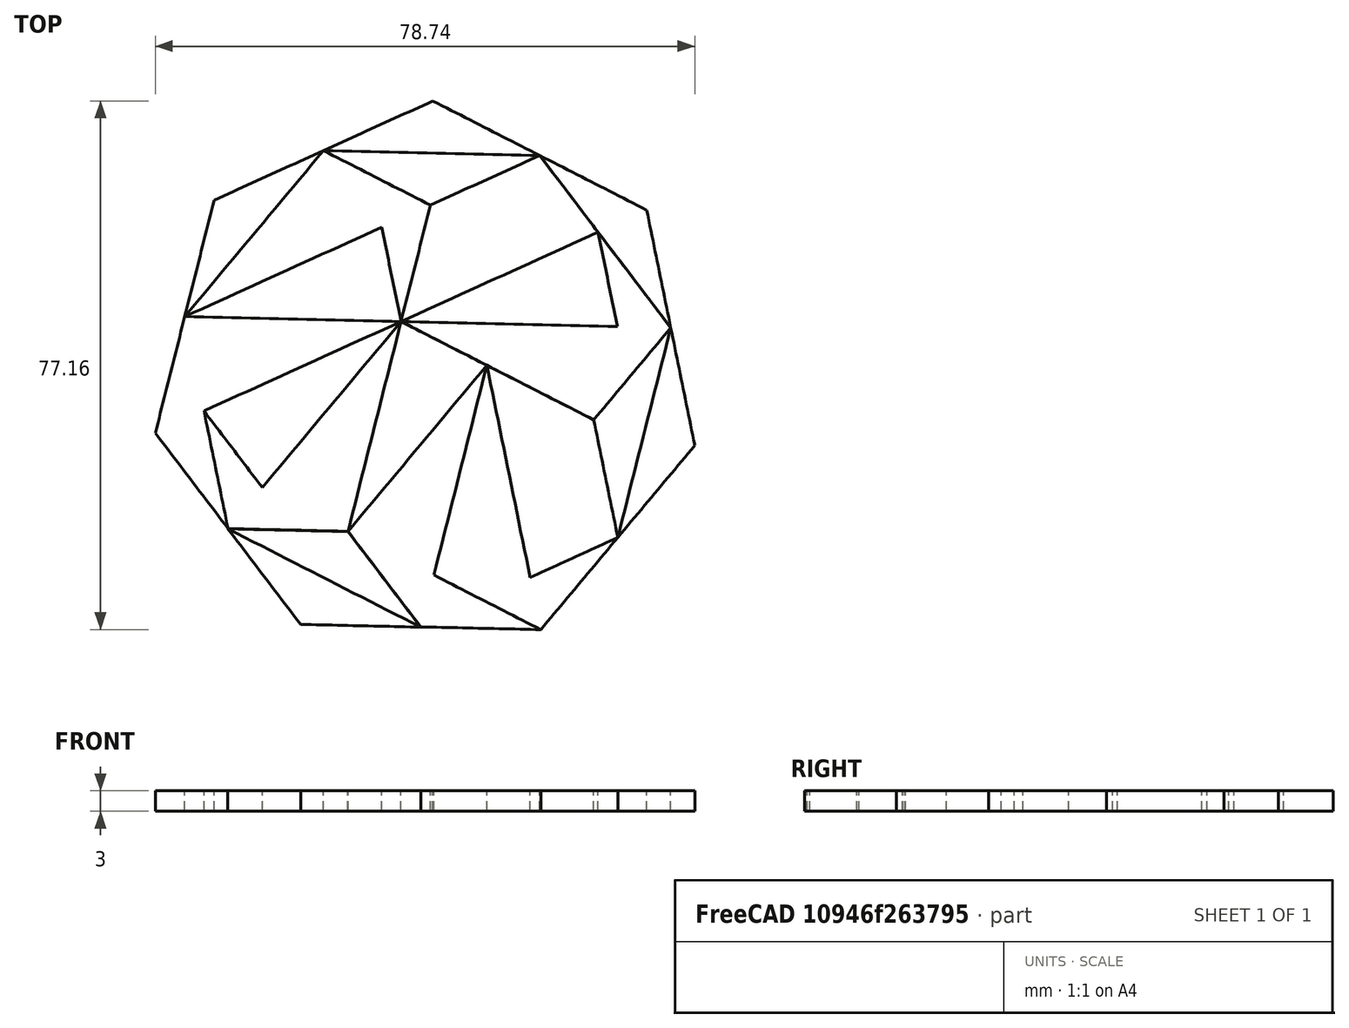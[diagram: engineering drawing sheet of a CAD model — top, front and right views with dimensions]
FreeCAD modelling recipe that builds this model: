
FCSTD DOCUMENT  (FreeCAD 0.17R13509 (Git))
Label: Puzle_Heptagono
License: CreativeCommons Attribution-ShareAlike
LicenseURL: http://creativecommons.org/licenses/by-sa/4.0/
objects: Part::Feature×20, Part::Extrusion×20
note: 40 computed .brp shape members not serialized (recipe doc carries the construction recipe); baked Part::Feature solids carry a one-line shape summary decoded from their .brp

FEATURE [Part::Feature] path28
  shape: bbox 28.13 x 38.58 x 2e-07 mm, 1 faces, 0 solids (baked)
FEATURE [Part::Feature] path34
  shape: bbox 26.85 x 38.58 x 2e-07 mm, 1 faces, 0 solids (baked)
FEATURE [Part::Feature] path40
  shape: bbox 28.76 x 30.62 x 2e-07 mm, 1 faces, 0 solids (baked)
FEATURE [Part::Feature] path46
  shape: bbox 28.76 x 24.23 x 2e-07 mm, 1 faces, 0 solids (baked)
FEATURE [Part::Feature] path52
  shape: bbox 31.57 x 13.77 x 2e-07 mm, 1 faces, 0 solids (baked)
FEATURE [Part::Feature] path58
  shape: bbox 31.57 x 13.77 x 2e-07 mm, 1 faces, 0 solids (baked)
FEATURE [Part::Feature] path64
  shape: bbox 35.86 x 30.94 x 2e-07 mm, 1 faces, 0 solids (baked)
FEATURE [Part::Feature] path70
  shape: bbox 20.25 x 30.62 x 2e-07 mm, 1 faces, 0 solids (baked)
FEATURE [Part::Feature] path76
  shape: bbox 19.12 x 30.94 x 2e-07 mm, 1 faces, 0 solids (baked)
FEATURE [Part::Feature] path82
  shape: bbox 11.24 x 30.62 x 2e-07 mm, 1 faces, 0 solids (baked)
FEATURE [Part::Feature] path88
  shape: bbox 11.24 x 30.62 x 2e-07 mm, 1 faces, 0 solids (baked)
FEATURE [Part::Feature] path94
  shape: bbox 39.37 x 27.4 x 2e-07 mm, 1 faces, 0 solids (baked)
FEATURE [Part::Feature] path100
  shape: bbox 19.12 x 25.13 x 2e-07 mm, 1 faces, 0 solids (baked)
FEATURE [Part::Feature] path106
  shape: bbox 28.76 x 24.23 x 2e-07 mm, 1 faces, 0 solids (baked)
FEATURE [Part::Feature] path112
  shape: bbox 35.86 x 24.95 x 2e-07 mm, 1 faces, 0 solids (baked)
FEATURE [Part::Feature] path124
  shape: bbox 20.25 x 24.23 x 2e-07 mm, 1 faces, 0 solids (baked)
FEATURE [Part::Feature] path118
  shape: bbox 31.9 x 20.87 x 2e-07 mm, 1 faces, 0 solids (baked)
FEATURE [Part::Feature] path130
  shape: bbox 28.13 x 14.35 x 2e-07 mm, 1 faces, 0 solids (baked)
FEATURE [Part::Feature] path5263
  shape: bbox 31.57 x 7.962 x 2e-07 mm, 1 faces, 0 solids (baked)
FEATURE [Part::Feature] path5269
  shape: bbox 31.57 x 7.962 x 2e-07 mm, 1 faces, 0 solids (baked)
FEATURE [Part::Extrusion] Extrude  label="Extrude01"
  Base = -> path28
  Dir = (0,0,1)
  DirMode = 0
  FaceMakerClass = Part::FaceMakerBullseye
  LengthFwd = 3
  LengthRev = 0
  Solid = false
  Symmetric = false
FEATURE [Part::Extrusion] Extrude001  label="Extrude02"
  Base = -> path34
  Dir = (0,0,1)
  DirMode = 0
  FaceMakerClass = Part::FaceMakerBullseye
  LengthFwd = 3
  LengthRev = 0
  Solid = false
  Symmetric = false
FEATURE [Part::Extrusion] Extrude002  label="Extrude03"
  Base = -> path40
  Dir = (0,0,1)
  DirMode = 0
  FaceMakerClass = Part::FaceMakerBullseye
  LengthFwd = 3
  LengthRev = 0
  Solid = false
  Symmetric = false
FEATURE [Part::Extrusion] Extrude003  label="Extrude04"
  Base = -> path46
  Dir = (0,0,1)
  DirMode = 0
  FaceMakerClass = Part::FaceMakerBullseye
  LengthFwd = 3
  LengthRev = 0
  Solid = false
  Symmetric = false
FEATURE [Part::Extrusion] Extrude004  label="Extrude05"
  Base = -> path52
  Dir = (0,0,1)
  DirMode = 0
  FaceMakerClass = Part::FaceMakerBullseye
  LengthFwd = 3
  LengthRev = 0
  Solid = false
  Symmetric = false
FEATURE [Part::Extrusion] Extrude005  label="Extrude06"
  Base = -> path58
  Dir = (0,0,1)
  DirMode = 0
  FaceMakerClass = Part::FaceMakerBullseye
  LengthFwd = 3
  LengthRev = 0
  Solid = false
  Symmetric = false
FEATURE [Part::Extrusion] Extrude006  label="Extrude07"
  Base = -> path64
  Dir = (0,0,1)
  DirMode = 0
  FaceMakerClass = Part::FaceMakerBullseye
  LengthFwd = 3
  LengthRev = 0
  Solid = false
  Symmetric = false
FEATURE [Part::Extrusion] Extrude007  label="Extrude08"
  Base = -> path70
  Dir = (0,0,1)
  DirMode = 0
  FaceMakerClass = Part::FaceMakerBullseye
  LengthFwd = 3
  LengthRev = 0
  Solid = false
  Symmetric = false
FEATURE [Part::Extrusion] Extrude008  label="Extrude09"
  Base = -> path76
  Dir = (0,0,1)
  DirMode = 0
  FaceMakerClass = Part::FaceMakerBullseye
  LengthFwd = 3
  LengthRev = 0
  Solid = false
  Symmetric = false
FEATURE [Part::Extrusion] Extrude009  label="Extrude10"
  Base = -> path82
  Dir = (0,0,1)
  DirMode = 0
  FaceMakerClass = Part::FaceMakerBullseye
  LengthFwd = 3
  LengthRev = 0
  Solid = false
  Symmetric = false
FEATURE [Part::Extrusion] Extrude010  label="Extrude11"
  Base = -> path88
  Dir = (0,0,1)
  DirMode = 0
  FaceMakerClass = Part::FaceMakerBullseye
  LengthFwd = 3
  LengthRev = 0
  Solid = false
  Symmetric = false
FEATURE [Part::Extrusion] Extrude011  label="Extrude12"
  Base = -> path94
  Dir = (0,0,1)
  DirMode = 0
  FaceMakerClass = Part::FaceMakerBullseye
  LengthFwd = 3
  LengthRev = 0
  Solid = false
  Symmetric = false
FEATURE [Part::Extrusion] Extrude012  label="Extrude13"
  Base = -> path100
  Dir = (0,0,1)
  DirMode = 0
  FaceMakerClass = Part::FaceMakerBullseye
  LengthFwd = 3
  LengthRev = 0
  Solid = false
  Symmetric = false
FEATURE [Part::Extrusion] Extrude013  label="Extrude14"
  Base = -> path106
  Dir = (0,0,1)
  DirMode = 0
  FaceMakerClass = Part::FaceMakerBullseye
  LengthFwd = 3
  LengthRev = 0
  Solid = false
  Symmetric = false
FEATURE [Part::Extrusion] Extrude014  label="Extrude15"
  Base = -> path112
  Dir = (0,0,1)
  DirMode = 0
  FaceMakerClass = Part::FaceMakerBullseye
  LengthFwd = 3
  LengthRev = 0
  Solid = false
  Symmetric = false
FEATURE [Part::Extrusion] Extrude015  label="Extrude16"
  Base = -> path124
  Dir = (0,0,1)
  DirMode = 0
  FaceMakerClass = Part::FaceMakerBullseye
  LengthFwd = 3
  LengthRev = 0
  Solid = false
  Symmetric = false
FEATURE [Part::Extrusion] Extrude016  label="Extrude17"
  Base = -> path118
  Dir = (0,0,1)
  DirMode = 0
  FaceMakerClass = Part::FaceMakerBullseye
  LengthFwd = 3
  LengthRev = 0
  Solid = false
  Symmetric = false
FEATURE [Part::Extrusion] Extrude017  label="Extrude18"
  Base = -> path130
  Dir = (0,0,1)
  DirMode = 0
  FaceMakerClass = Part::FaceMakerBullseye
  LengthFwd = 3
  LengthRev = 0
  Solid = false
  Symmetric = false
FEATURE [Part::Extrusion] Extrude091  label="Extrude19"
  Base = -> path5263
  Dir = (0,0,1)
  DirMode = 0
  FaceMakerClass = Part::FaceMakerBullseye
  LengthFwd = 3
  LengthRev = 0
  Solid = false
  Symmetric = false
FEATURE [Part::Extrusion] Extrude092  label="Extrude20"
  Base = -> path5269
  Dir = (0,0,1)
  DirMode = 0
  FaceMakerClass = Part::FaceMakerBullseye
  LengthFwd = 3
  LengthRev = 0
  Solid = false
  Symmetric = false
